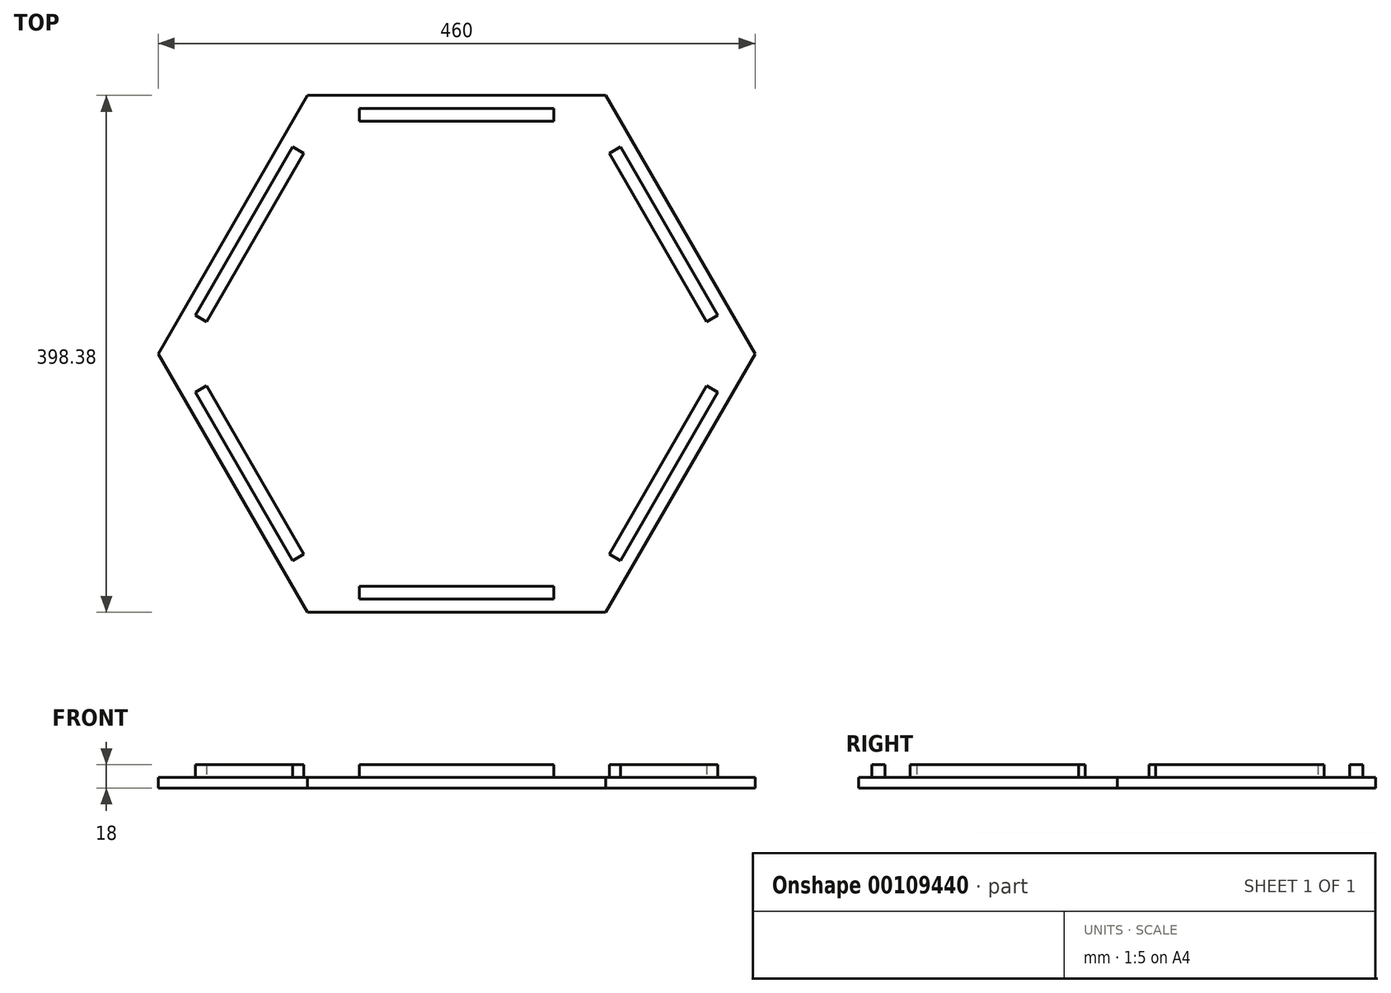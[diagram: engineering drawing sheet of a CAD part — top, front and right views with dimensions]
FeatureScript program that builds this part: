
annotation { "Feature Type Name" : "Feature", "Feature Type Description" : "" }
export const myFeature = defineFeature(function(context is Context, id is Id, definition is map)
    precondition{}
    {
        {
            var Q0;
            Q0=qCreatedBy(makeId("Top.planeOp"),FACE);
            var sketch = newSketch(context, id + "F0", { "sketchPlane" : qUnion([Q0])});
            skCircle(sketch, "E0.cCircle", {"center": v(0, 0) * mm, "radius": 199.19 * mm, "construction": true});
            skLineSegment(sketch, "E0.0", {"start": v(115, -199.19) * mm, "end": v(-115, -199.19) * mm});
            skLineSegment(sketch, "E0.1", {"start": v(-115, -199.19) * mm, "end": v(-230, 0) * mm});
            skLineSegment(sketch, "E0.2", {"start": v(-230, 0) * mm, "end": v(-115, 199.19) * mm});
            skLineSegment(sketch, "E0.3", {"start": v(-115, 199.19) * mm, "end": v(115, 199.19) * mm});
            skLineSegment(sketch, "E0.4", {"start": v(115, 199.19) * mm, "end": v(230, 0) * mm});
            skLineSegment(sketch, "E0.5", {"start": v(230, 0) * mm, "end": v(115, -199.19) * mm});
            skPoint(sketch, "E0.0.midPoint", {"position": v(0, -199.19) * mm});
            skSolve(sketch);
        }
        {
            var Q0;
            Q0 = qSketchRegion(id + "F0", true);
            extrude(context, id + "F1", {"entities" : qUnion([Q0]), "depth" : 8 * mm});
        }
        {
            var Q0;
            Q0=makeQuery(id+"F1.opExtrude","CAP_FACE",FACE,{"disambiguationData":[OSD([sQuery(id+"F0.wireOp",EDGE,"E0.0"),sQuery(id+"F0.wireOp",EDGE,"E0.1"),sQuery(id+"F0.wireOp",EDGE,"E0.2"),sQuery(id+"F0.wireOp",EDGE,"E0.3"),sQuery(id+"F0.wireOp",EDGE,"E0.4"),sQuery(id+"F0.wireOp",EDGE,"E0.5")])],"isStart":false});
            var sketch = newSketch(context, id + "F2", { "sketchPlane" : qUnion([Q0])});
            skLineSegment(sketch, "E1.bottom", {"start": v(-75, 189.19) * mm, "end": v(75, 189.19) * mm});
            skLineSegment(sketch, "E1.top", {"start": v(-75, 179.19) * mm, "end": v(75, 179.19) * mm});
            skLineSegment(sketch, "E1.left", {"start": v(-75, 189.19) * mm, "end": v(-75, 179.19) * mm});
            skLineSegment(sketch, "E1.right", {"start": v(75, 189.19) * mm, "end": v(75, 179.19) * mm});
            skLineSegment(sketch, "E2", {"start": v(0, 179.19) * mm, "end": v(0, 0) * mm, "construction": true});
            skSolve(sketch);
        }
        {
            var Q0;
            Q0 = qSketchRegion(id + "F2", true);
            extrude(context, id + "F3", {"entities" : qUnion([Q0]), "depth" : 10 * mm});
        }
        {
            var Q0;
            Q0=qCreatedBy(makeId("Right.planeOp"),FACE);
            var sketch = newSketch(context, id + "F4", { "sketchPlane" : qUnion([Q0])});
            skLineSegment(sketch, "E3", {"start": v(0, 0) * mm, "end": v(0, 118.99) * mm, "construction": true});
            skSolve(sketch);
        }
        {
            var Q0;
            Q0=makeQuery(id+"F3.opExtrude","SWEPT_BODY",BODY,{"disambiguationData":[OSD([sQuery(id+"F2.wireOp",EDGE,"E1.bottom"),sQuery(id+"F2.wireOp",EDGE,"E1.top"),sQuery(id+"F2.wireOp",EDGE,"E1.left"),sQuery(id+"F2.wireOp",EDGE,"E1.right")])]});
            var Q1;
            Q1=sQuery(id+"F4.wireOp",EDGE,"E3");
            circularPattern(context, id + "F5", {"entities" : qUnion([Q0]), "axis" : qUnion([Q1]), "angle" : 60 * degree, "instanceCount" : 6});
        }
    });
